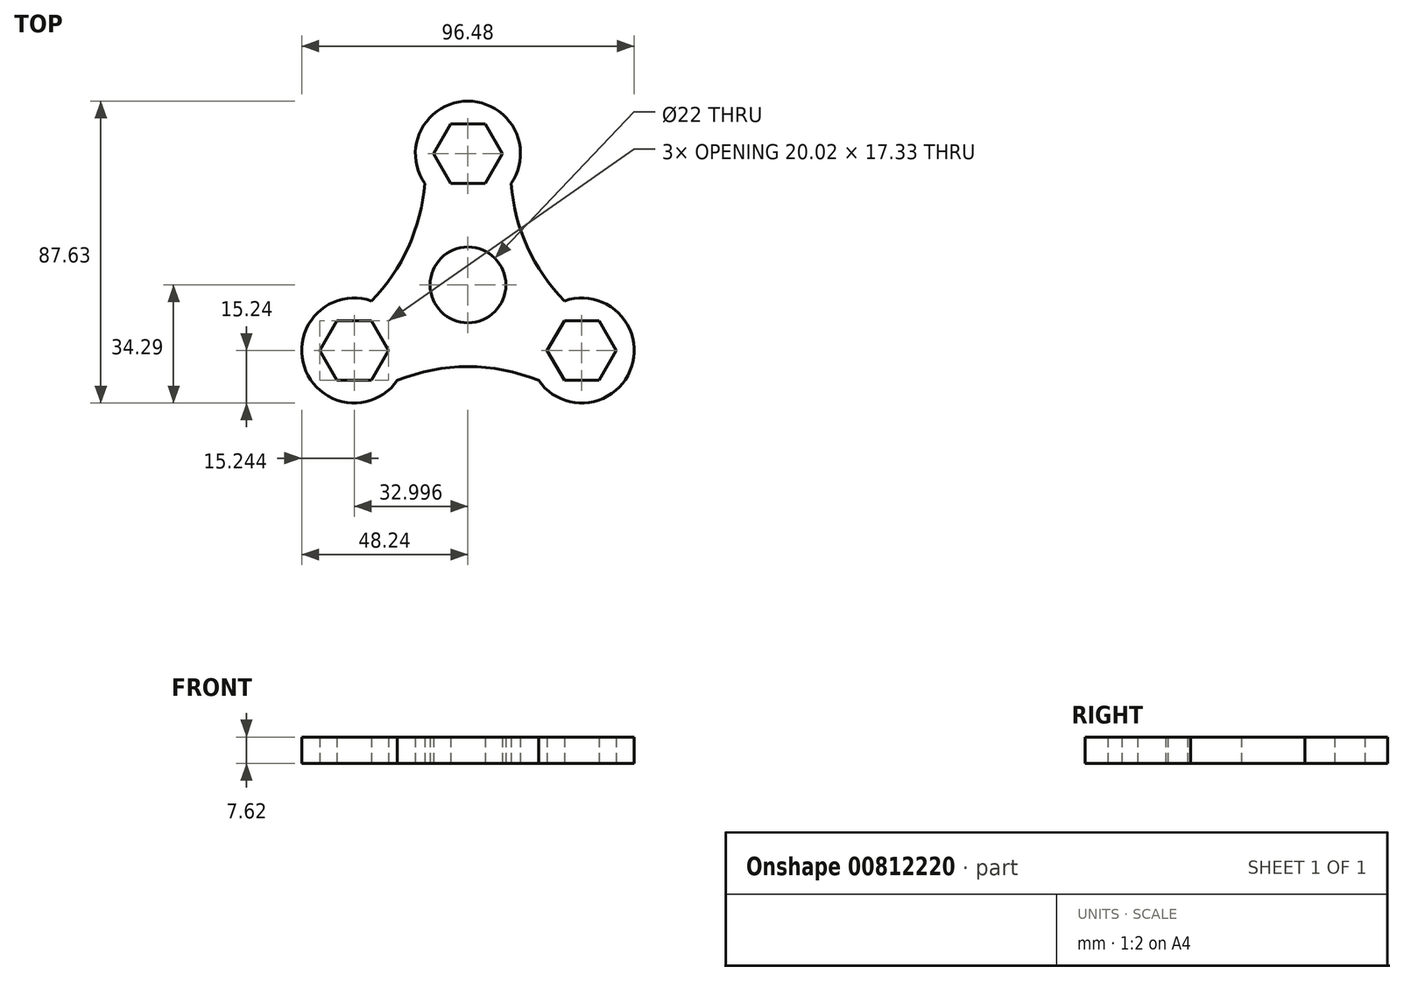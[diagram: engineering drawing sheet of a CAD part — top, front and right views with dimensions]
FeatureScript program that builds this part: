
annotation { "Feature Type Name" : "Feature", "Feature Type Description" : "" }
export const myFeature = defineFeature(function(context is Context, id is Id, definition is map)
    precondition{}
    {
        {
            var Q0;
            Q0=qCreatedBy(makeId("Top.planeOp"),FACE);
            var sketch = newSketch(context, id + "F0", { "sketchPlane" : qUnion([Q0])});
            skLineSegment(sketch, "E0", {"start": v(0, 0) * mm, "end": v(0, 38.1) * mm});
            skLineSegment(sketch, "E1", {"start": v(0, 0) * mm, "end": v(-33, -19.05) * mm});
            skLineSegment(sketch, "E2", {"start": v(0, 0) * mm, "end": v(33, -19.05) * mm});
            skCircle(sketch, "E3.cCircle", {"center": v(0, 38.1) * mm, "radius": 8.67 * mm, "construction": true});
            skLineSegment(sketch, "E3.0", {"start": v(-5, 46.77) * mm, "end": v(5, 46.77) * mm});
            skLineSegment(sketch, "E3.1", {"start": v(5, 46.77) * mm, "end": v(10, 38.1) * mm});
            skLineSegment(sketch, "E3.2", {"start": v(10, 38.1) * mm, "end": v(5, 29.43) * mm});
            skLineSegment(sketch, "E3.3", {"start": v(5, 29.43) * mm, "end": v(-5, 29.43) * mm});
            skLineSegment(sketch, "E3.4", {"start": v(-5, 29.43) * mm, "end": v(-10, 38.1) * mm});
            skLineSegment(sketch, "E3.5", {"start": v(-10, 38.1) * mm, "end": v(-5, 46.77) * mm});
            skPoint(sketch, "E3.0.midPoint", {"position": v(0, 46.77) * mm});
            skCircle(sketch, "E4.cCircle", {"center": v(-33, -19.05) * mm, "radius": 8.67 * mm, "construction": true});
            skLineSegment(sketch, "E4.0", {"start": v(-38, -10.38) * mm, "end": v(-28, -10.38) * mm});
            skLineSegment(sketch, "E4.1", {"start": v(-28, -10.38) * mm, "end": v(-22.99, -19.05) * mm});
            skLineSegment(sketch, "E4.2", {"start": v(-22.99, -19.05) * mm, "end": v(-28, -27.72) * mm});
            skLineSegment(sketch, "E4.3", {"start": v(-28, -27.72) * mm, "end": v(-38, -27.72) * mm});
            skLineSegment(sketch, "E4.4", {"start": v(-38, -27.72) * mm, "end": v(-43, -19.05) * mm});
            skLineSegment(sketch, "E4.5", {"start": v(-43, -19.05) * mm, "end": v(-38, -10.38) * mm});
            skPoint(sketch, "E4.0.midPoint", {"position": v(-33, -10.38) * mm});
            skCircle(sketch, "E5.cCircle", {"center": v(33, -19.05) * mm, "radius": 8.67 * mm, "construction": true});
            skLineSegment(sketch, "E5.0", {"start": v(43, -19.05) * mm, "end": v(38, -27.72) * mm});
            skLineSegment(sketch, "E5.1", {"start": v(38, -27.72) * mm, "end": v(28, -27.72) * mm});
            skLineSegment(sketch, "E5.2", {"start": v(28, -27.72) * mm, "end": v(22.99, -19.05) * mm});
            skLineSegment(sketch, "E5.3", {"start": v(22.99, -19.05) * mm, "end": v(28, -10.38) * mm});
            skLineSegment(sketch, "E5.4", {"start": v(28, -10.38) * mm, "end": v(38, -10.38) * mm});
            skLineSegment(sketch, "E5.5", {"start": v(38, -10.38) * mm, "end": v(43, -19.05) * mm});
            skPoint(sketch, "E5.0.midPoint", {"position": v(40.5, -23.38) * mm});
            skCircle(sketch, "E6", {"center": v(0, 38.1) * mm, "radius": 15.24 * mm});
            skCircle(sketch, "E7", {"center": v(-33, -19.05) * mm, "radius": 15.24 * mm});
            skCircle(sketch, "E8", {"center": v(33, -19.05) * mm, "radius": 15.24 * mm});
            skCircle(sketch, "E9", {"center": v(0, 0) * mm, "radius": 11 * mm});
            skArc(sketch, "E10", {"start": v(-28, -4.65) * mm, "mid": v(-17.25, 11.02) * mm, "end": v(-12.54, 29.43) * mm});
            skArc(sketch, "E11", {"start": v(12.54, 29.43) * mm, "mid": v(17.25, 11.02) * mm, "end": v(28, -4.65) * mm});
            skArc(sketch, "E12", {"start": v(20.46, -27.72) * mm, "mid": v(0, -23.74) * mm, "end": v(-20.46, -27.72) * mm});
            skSolve(sketch);
        }
        {
            var Q0;
            Q0=makeQuery(id+"F0.imprint","IMPRINT",FACE,{"disambiguationData":[TD([[makeQuery(id+"F0.imprint","IMPRINT",EDGE,{"derivedFrom":sQuery(id+"F0.wireOp",EDGE,"E3.0")}),1.0]])]});
            var Q1;
            {var subQ0=sQuery(id+"F0.wireOp",EDGE,"xFhrTNdy-n9Ld-Rqk0-firn-8koVEWlA8PZZ");Q1=makeQuery(id+"F0.imprint","IMPRINT",FACE,{"disambiguationData":[TD([[makeQuery(id+"F0.imprint","IMPRINT",EDGE,{"derivedFrom":subQ0}),-1.0]])]});}
            var Q2;
            {var subQ0=sQuery(id+"F0.wireOp",EDGE,"4QsZ0Ccn-dia0-sdtq-Yh0d-z4021OBEYiar");Q2=makeQuery(id+"F0.imprint","IMPRINT",FACE,{"disambiguationData":[TD([[makeQuery(id+"F0.imprint","IMPRINT",EDGE,{"derivedFrom":subQ0}),-1.0]])]});}
            var Q3;
            {var subQ0=sQuery(id+"F0.wireOp",EDGE,"nWyzpXpm-jD31-eREV-zhh0-6CstPiLFMHhk");Q3=makeQuery(id+"F0.imprint","IMPRINT",FACE,{"disambiguationData":[TD([[makeQuery(id+"F0.imprint","IMPRINT",EDGE,{"derivedFrom":subQ0}),-1.0]])]});}
            var Q4;
            Q4=makeQuery(id+"F0.imprint","IMPRINT",FACE,{"disambiguationData":[TD([[makeQuery(id+"F0.imprint","IMPRINT",EDGE,{"derivedFrom":sQuery(id+"F0.wireOp",EDGE,"E5.0")}),1.0]])]});
            var Q5;
            {var subQ3=sQuery(id+"F0.wireOp",EDGE,"E4.0");Q5=makeQuery(id+"F0.imprint","IMPRINT",FACE,{"disambiguationData":[TD([[makeQuery(id+"F0.imprint","IMPRINT",EDGE,{"derivedFrom":subQ3}),1.0]])]});}
            var Q6;
            {var subQ0=sQuery(id+"F0.wireOp",EDGE,"9NHwrqiA-zxWA-xh7g-7E73-jBwCxU8Xtf1k");Q6=makeQuery(id+"F0.imprint","IMPRINT",FACE,{"disambiguationData":[TD([[makeQuery(id+"F0.imprint","IMPRINT",EDGE,{"derivedFrom":subQ0}),-1.0]])]});}
            var Q7;
            {var subQ0=sQuery(id+"F0.wireOp",EDGE,"NzF22WQF-SIZO-UqOH-Meyj-5mhhmQmQIhMc");Q7=makeQuery(id+"F0.imprint","IMPRINT",FACE,{"disambiguationData":[TD([[makeQuery(id+"F0.imprint","IMPRINT",EDGE,{"derivedFrom":subQ0}),-1.0]])]});}
            var Q8;
            {var subQ0=sQuery(id+"F0.wireOp",EDGE,"07XtHqp4-dNtp-Ns72-P1Sj-wY0c2Bpn3Mhl");Q8=makeQuery(id+"F0.imprint","IMPRINT",FACE,{"disambiguationData":[TD([[makeQuery(id+"F0.imprint","IMPRINT",EDGE,{"derivedFrom":subQ0}),-1.0]])]});}
            var Q9;
            {var subQ0=sQuery(id+"F0.wireOp",EDGE,"E10");Q9=makeQuery(id+"F0.imprint","IMPRINT",FACE,{"disambiguationData":[TD([[makeQuery(id+"F0.imprint","IMPRINT",EDGE,{"derivedFrom":subQ0}),-1.0]])]});}
            var Q10;
            {var subQ0=sQuery(id+"F0.wireOp",EDGE,"E11");Q10=makeQuery(id+"F0.imprint","IMPRINT",FACE,{"disambiguationData":[TD([[makeQuery(id+"F0.imprint","IMPRINT",EDGE,{"derivedFrom":subQ0}),-1.0]])]});}
            var Q11;
            {var subQ0=sQuery(id+"F0.wireOp",EDGE,"E12");Q11=makeQuery(id+"F0.imprint","IMPRINT",FACE,{"disambiguationData":[TD([[makeQuery(id+"F0.imprint","IMPRINT",EDGE,{"derivedFrom":subQ0}),-1.0]])]});}
            extrude(context, id + "F1", {"entities" : qUnion([Q0, Q1, Q2, Q3, Q4, Q5, Q6, Q7, Q8, Q9, Q10, Q11]), "depth" : 7.62 * mm, "offsetDistance" : 25.4 * mm});
        }
    });
